# Revit family: Mechanism_Kit-Mini_Tower-Simon-500_CIMA
name_source: partatom
category: Electrical Fixtures
revit_build: Autodesk Revit 2014 (Build: 20130308_1515(x64)
units: mm (PartAtom-declared; Revit-internal decimal feet)

## types (1)
- 3 Modules, Metal
    Box Type = Null Connect
    Cost = 123.99€
    Current = 16 A
    D3 = 63 mm
    D4 = 126 mm
    Default Elevation = 1219 mm
    Description = UPS 1-face metal mini-tower kit with 1 double Schuko outlet, 1 double UPS Schuko outlet and 2 V&D plates for 1 RJ45 connector.
    Element Material = Grey Finish
    Frame Offset = 57 mm
    Frame Type = Frame Connect Metal Tower
    Height = 236 mm
    Kit Material = Stainless Steel, Brushed
    Manufacturer = SIMON
    Manufacturing material = Aluminium structure and stainless steel frame (AISI 430 ferritic stainless steel type)
    Mini-Tower Depth = 68 mm
    Model = 52516302-036
    Overall dimensions = 236x168 mm
    Protection against impacts = IK10
    Protection against solid and liquid bodies = IP40
    RJ45 compatibility figure = Keystone I, II and Systimax
    Series = Simon 500 CIMA
    Technical data sheet = http://www.simon.es
    URL = http://www.simon.es
    Voice and data connectors type = RJ45
    e2 = Null Connect
    e4 = Double Data
    n = 2

## geometry (parser evidence)
native form markers: Blend x6
no freeform markers — native parametric forms only
